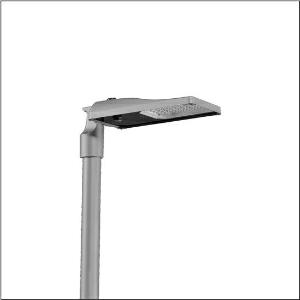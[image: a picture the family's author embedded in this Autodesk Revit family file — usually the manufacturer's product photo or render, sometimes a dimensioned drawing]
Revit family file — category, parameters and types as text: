
# Revit family: streetlight_sl_31_mini___st1_0a_5xh2d71t08ga_b82e
name_source: partatom
category: Lighting Fixtures
units: mm (PartAtom-declared; Revit-internal decimal feet)

## family parameters
Cut with Voids When Loaded = No
Host = Face
Light Source = No
Part Type = Normal
Room Calculation Point = No
Round Connector Dimension = Use Diameter
Shared = No

## types (1)
- --- (1 x LED, 4860 lm, 39.3 W, 2200K)
    Apparent Load = 39 VA
    CIE Flux Codes = 37 72 97 100 100
    Color Rendering = 70
    Color Temperature = 2200K
    Default Elevation = 1800 mm
    Description = Streetlight SL 31 mini, mast luminaire, primary light control with lens, of PMMA, primary optical cover: cover, of toughened safety glass, transparent, light distribution: ST1.0a, light emission: direct distribution, primary light characteristic: asymmetric, installation type: post-top, side-entry, LED, High Power LED, rated luminous flux: 4.860lm, luminous efficacy: 124lm/W, light colour: 722, colour temperature: 2200K, control: presetting dimming logarithmic, flexible luminous flux parameterisation, time-dependent luminous flux control, constant luminous flux control, power reduction, intelligent temperature release in ECG and LED module, overheat protection, with cable H07RN-F 2x 1.5mm², mains connection: 220..240V, AC, 50/60Hz, connection cable pre-assembled, cable length: 6,5m, start of lifetime: 39W, end of service life: 41W, reduction: 18W, luminaire housing, of diecast aluminium, powder-coated, Siteco® metallic grey (DB 702S), corrosivity category C5 high according to DIN EN ISO 12944, no sealing on luminaire upper side, inclination: -15°..+20° (post-top) | -20°..+20° (side-entry), adjustable in 5° steps, mast flange (76/60mm) included as standard, multi-level sealing system, sealing non-destructively replaceable, Smart Interface below and above, protection rating (complete): IP66, insulation class (complete): insulation class II (safety insulation), certification: CE, ENEC, ENEC+, VDE, UKCA, ZD4i, impact resistance: IK09, permissible operating ambient temperature for outdoor applications: -40..+50°C, standard-compliant lighting for roads and squares, packaging unit: 1 piece

Light Distribution: ST1.0a
    Height = 76 mm
    Lamp = 1 x LED
    Lamp Light Flux = 4860 lm
    Lamp Power = 39.3 W
    Lamp count = 1
    Length = 547 mm
    Luminous efficacy = 124 lm/W
    Manufacturer = Siteco
    ModVariant = No
    Model = 5XH2D71T08GA
    Number of Poles = 1
    OnlyDefault = Yes
    Power Factor = 1
    Product Name = Streetlight SL 31 mini | ST1.0a
    Product group = mast luminaire | pylon top
    ProductGroupID = 6100
    Protection Class = Protection class II
    Protection Degree = IP 66
    RLX_Detail_Level = 1
    RLX_Emergency_Light_Flux = 0 lm
    RLX_Emergency_Type = 0
    RLX_Emergency_Type_DB = No
    RlxData = <blob elided: 40057 chars, md5=63dbcf36>
    Socket = socket
    Standby Power = 0 W
    System Light Flux = 4860 lm
    System Power = 39 W
    Type Comments = factory setting: luminous flux: 100 % | dim-lin: 254 | 798 mA
    Type Image = l_1300332.jpg
    URL = http://relux.com
    VarID = @adj_012883
    Voltage = 0 V
    Weight = 0.00 kg
    Width = 265 mm

## geometry (parser evidence)
native form markers: Blend x4, Sweep x10
no freeform markers — native parametric forms only
